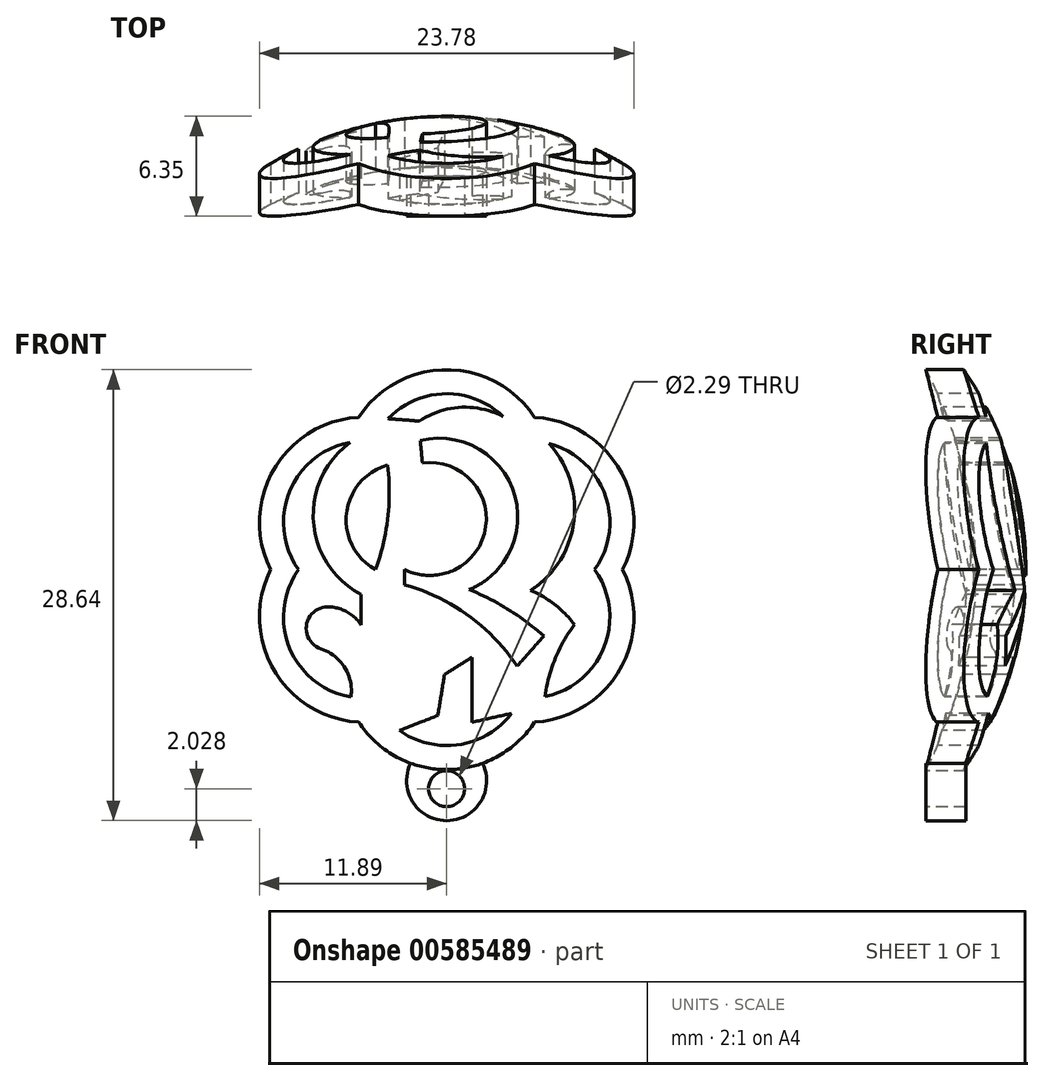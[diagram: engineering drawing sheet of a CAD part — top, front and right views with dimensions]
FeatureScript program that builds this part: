
annotation { "Feature Type Name" : "Feature", "Feature Type Description" : "" }
export const myFeature = defineFeature(function(context is Context, id is Id, definition is map)
    precondition{}
    {
        {
            var Q0;
            Q0=qCreatedBy(makeId("Top.planeOp"),FACE);
            var sketch = newSketch(context, id + "F0", { "sketchPlane" : qUnion([Q0])});
            skArc(sketch, "E0", {"start": v(0, 3.18) * mm, "mid": v(-6.55, 2.37) * mm, "end": v(-12.7, 0) * mm});
            skArc(sketch, "E1", {"start": v(0, 6.35) * mm, "mid": v(-6.65, 5.34) * mm, "end": v(-12.7, 2.4) * mm});
            skLineSegment(sketch, "E2", {"start": v(0, 6.35) * mm, "end": v(0, 3.18) * mm});
            skLineSegment(sketch, "E3", {"start": v(-12.7, 0) * mm, "end": v(-12.7, 2.4) * mm});
            skLineSegment(sketch, "E4", {"start": v(0, 6.35) * mm, "end": v(8.6, 6.35) * mm, "construction": true});
            skLineSegment(sketch, "E5", {"start": v(0, 3.18) * mm, "end": v(5.54, 3.18) * mm, "construction": true});
            skSolve(sketch);
        }
        {
            var Q0;
            Q0=makeQuery(id+"F0.imprint","IMPRINT",FACE,{"disambiguationData":[TD([[makeQuery(id+"F0.imprint","IMPRINT",EDGE,{"derivedFrom":sQuery(id+"F0.wireOp",EDGE,"E0")}),-1.0]])]});
            var Q1;
            Q1=sQuery(id+"F0.wireOp",EDGE,"E2");
            revolve(context, id + "F1", {"entities" : qUnion([Q0]), "axis" : qUnion([Q1]), "revolveType" : RevolveType.FULL});
        }
        {
            var Q0;
            Q0=qCreatedBy(makeId("Front.planeOp"),FACE);
            var sketch = newSketch(context, id + "F2", { "sketchPlane" : qUnion([Q0])});
            skCircle(sketch, "E6.cCircle", {"center": v(0, 0) * mm, "radius": 9.68 * mm, "construction": true});
            skLineSegment(sketch, "E6.0", {"start": v(5.59, -9.68) * mm, "end": v(-5.59, -9.68) * mm, "construction": true});
            skLineSegment(sketch, "E6.1", {"start": v(-5.59, -9.68) * mm, "end": v(-11.18, 0) * mm, "construction": true});
            skLineSegment(sketch, "E6.2", {"start": v(-11.18, 0) * mm, "end": v(-5.59, 9.68) * mm, "construction": true});
            skLineSegment(sketch, "E6.3", {"start": v(-5.59, 9.68) * mm, "end": v(5.59, 9.68) * mm, "construction": true});
            skLineSegment(sketch, "E6.4", {"start": v(5.59, 9.68) * mm, "end": v(11.18, 0) * mm, "construction": true});
            skLineSegment(sketch, "E6.5", {"start": v(11.18, 0) * mm, "end": v(5.59, -9.68) * mm, "construction": true});
            skPoint(sketch, "E6.0.midPoint", {"position": v(0, -9.68) * mm});
            skArc(sketch, "E7", {"start": v(-5.59, -9.68) * mm, "mid": v(0, -12.7) * mm, "end": v(5.59, -9.68) * mm});
            skArc(sketch, "E8", {"start": v(5.59, -9.68) * mm, "mid": v(11, -6.35) * mm, "end": v(11.18, 0) * mm});
            skArc(sketch, "E9", {"start": v(11.18, 0) * mm, "mid": v(11, 6.35) * mm, "end": v(5.59, 9.68) * mm});
            skArc(sketch, "E10", {"start": v(5.59, 9.68) * mm, "mid": v(0, 12.7) * mm, "end": v(-5.59, 9.68) * mm});
            skArc(sketch, "E11", {"start": v(-5.59, 9.68) * mm, "mid": v(-11, 6.35) * mm, "end": v(-11.18, 0) * mm});
            skArc(sketch, "E12", {"start": v(-11.18, 0) * mm, "mid": v(-11, -6.35) * mm, "end": v(-5.59, -9.68) * mm});
            skSolve(sketch);
        }
        {
            var Q0;
            Q0 = qSketchRegion(id + "F2", true);
            extrude(context, id + "F3", {"entities" : qUnion([Q0]), "operationType" : NewBodyOperationType.INTERSECT, "oppositeDirection" : true, "depth" : 25.4 * mm, "offsetDistance" : 25.4 * mm});
        }
        {
            var Q0;
            Q0=qCreatedBy(makeId("Front.planeOp"),FACE);
            var sketch = newSketch(context, id + "F4", { "sketchPlane" : qUnion([Q0])});
            skArc(sketch, "E13", {"start": v(-3, -10.21) * mm, "mid": v(0.77, -11.12) * mm, "end": v(4.1, -9.13) * mm});
            skArc(sketch, "E14", {"start": v(6.24, -8.06) * mm, "mid": v(10.01, -4.9) * mm, "end": v(9.4, 0) * mm});
            skArc(sketch, "E15", {"start": v(9.4, 0) * mm, "mid": v(10.06, 4.77) * mm, "end": v(6.49, 8) * mm});
            skArc(sketch, "E16", {"start": v(5.34, -1.3) * mm, "mid": v(8.08, 3.08) * mm, "end": v(6.49, 8) * mm});
            skArc(sketch, "E17", {"start": v(-9.4, 0) * mm, "mid": v(-9.98, -4.97) * mm, "end": v(-6.08, -8.1) * mm});
            skArc(sketch, "E18", {"start": v(-6.13, 8.08) * mm, "mid": v(-10, 4.94) * mm, "end": v(-9.4, 0) * mm});
            skArc(sketch, "E19", {"start": v(3.58, 9.73) * mm, "mid": v(-0.1, 11.18) * mm, "end": v(-3.72, 9.6) * mm});
            skArc(sketch, "E20", {"start": v(3.58, 9.73) * mm, "mid": v(0.88, 10.31) * mm, "end": v(-1.73, 9.44) * mm});
            skLineSegment(sketch, "E21", {"start": v(-1.73, 9.44) * mm, "end": v(-3.72, 9.6) * mm});
            skArc(sketch, "E22", {"start": v(8.12, -3.5) * mm, "mid": v(6.87, -2.22) * mm, "end": v(5.34, -1.3) * mm});
            skArc(sketch, "E23", {"start": v(8.12, -3.5) * mm, "mid": v(6.9, -5.66) * mm, "end": v(6.24, -8.06) * mm});
            skLineSegment(sketch, "E24", {"start": v(-3, -10.21) * mm, "end": v(-0.55, -9.26) * mm});
            skLineSegment(sketch, "E25", {"start": v(-0.55, -9.26) * mm, "end": v(-0.14, -6.67) * mm});
            skLineSegment(sketch, "E26", {"start": v(-0.14, -6.67) * mm, "end": v(1.6, -5.57) * mm});
            skLineSegment(sketch, "E27", {"start": v(1.6, -5.57) * mm, "end": v(1.6, -9.69) * mm});
            skLineSegment(sketch, "E28", {"start": v(1.6, -9.69) * mm, "end": v(4.1, -9.13) * mm});
            skArc(sketch, "E29", {"start": v(-6.13, 8.08) * mm, "mid": v(-8.46, 3.06) * mm, "end": v(-5.43, -1.58) * mm});
            skLineSegment(sketch, "E30", {"start": v(-5.43, -1.58) * mm, "end": v(-5.43, -3.5) * mm});
            skArc(sketch, "E31", {"start": v(-6.08, -8.1) * mm, "mid": v(-6.47, -6.21) * mm, "end": v(-7.98, -5.03) * mm});
            skArc(sketch, "E32", {"start": v(-7.57, -2.36) * mm, "mid": v(-8.9, -3.52) * mm, "end": v(-7.98, -5.03) * mm});
            skArc(sketch, "E33", {"start": v(-5.43, -3.5) * mm, "mid": v(-6.36, -2.66) * mm, "end": v(-7.57, -2.36) * mm});
            skSolve(sketch);
        }
        {
            var Q0;
            Q0 = qSketchRegion(id + "F4", true);
            extrude(context, id + "F5", {"entities" : qUnion([Q0]), "operationType" : NewBodyOperationType.REMOVE, "oppositeDirection" : true, "depth" : 25.4 * mm, "offsetDistance" : 25.4 * mm});
        }
        {
            var Q0;
            Q0=qCreatedBy(makeId("Front.planeOp"),FACE);
            var sketch = newSketch(context, id + "F6", { "sketchPlane" : qUnion([Q0])});
            skArc(sketch, "E34", {"start": v(-3.74, 6.65) * mm, "mid": v(-6.36, 3.59) * mm, "end": v(-4.52, 0) * mm});
            skArc(sketch, "E35", {"start": v(-4.52, 0) * mm, "mid": v(-3.74, 3.28) * mm, "end": v(-3.74, 6.65) * mm});
            skSolve(sketch);
        }
        {
            var Q0;
            Q0=qCreatedBy(makeId("Front.planeOp"),FACE);
            var sketch = newSketch(context, id + "F7", { "sketchPlane" : qUnion([Q0])});
            skArc(sketch, "E36", {"start": v(4.48, -6.12) * mm, "mid": v(1.36, -2.9) * mm, "end": v(-2.67, -0.96) * mm});
            skLineSegment(sketch, "E37", {"start": v(-2.67, -0.96) * mm, "end": v(-2.67, 0) * mm});
            skLineSegment(sketch, "E38", {"start": v(4.48, -6.12) * mm, "end": v(6.17, -4.2) * mm});
            skArc(sketch, "E39", {"start": v(6.17, -4.2) * mm, "mid": v(3.93, -2.54) * mm, "end": v(1.43, -1.27) * mm});
            skArc(sketch, "E40", {"start": v(1.43, -1.27) * mm, "mid": v(4.27, 4.91) * mm, "end": v(-1.68, 8.2) * mm});
            skArc(sketch, "E41", {"start": v(-2.67, 0) * mm, "mid": v(2.47, 2.63) * mm, "end": v(-1.54, 6.78) * mm});
            skLineSegment(sketch, "E42", {"start": v(-1.54, 6.78) * mm, "end": v(-1.68, 8.2) * mm});
            skSolve(sketch);
        }
        {
            var Q0;
            Q0 = qSketchRegion(id + "F6", true);
            extrude(context, id + "F8", {"entities" : qUnion([Q0]), "operationType" : NewBodyOperationType.REMOVE, "oppositeDirection" : true, "depth" : 25.4 * mm, "offsetDistance" : 25.4 * mm});
        }
        {
            var Q0;
            Q0 = qSketchRegion(id + "F7", true);
            extrude(context, id + "F9", {"entities" : qUnion([Q0]), "operationType" : NewBodyOperationType.REMOVE, "oppositeDirection" : true, "depth" : 25.4 * mm, "offsetDistance" : 25.4 * mm});
        }
        {
            var Q0;
            Q0=qCreatedBy(makeId("Front.planeOp"),FACE);
            var sketch = newSketch(context, id + "F10", { "sketchPlane" : qUnion([Q0])});
            skCircle(sketch, "E43", {"center": v(0, -13.91) * mm, "radius": 1.14 * mm});
            skArc(sketch, "E44", {"start": v(-2.29, -12.3) * mm, "mid": v(0, -15.94) * mm, "end": v(2.29, -12.3) * mm});
            skArc(sketch, "E45", {"start": v(-2.29, -12.3) * mm, "mid": v(0, -12.7) * mm, "end": v(2.29, -12.3) * mm});
            skSolve(sketch);
        }
        {
            var Q0;
            Q0 = qSketchRegion(id + "F10", true);
            extrude(context, id + "F11", {"entities" : qUnion([Q0]), "operationType" : NewBodyOperationType.ADD, "oppositeDirection" : true, "depth" : 2.54 * mm, "offsetDistance" : 25.4 * mm});
        }
    });
